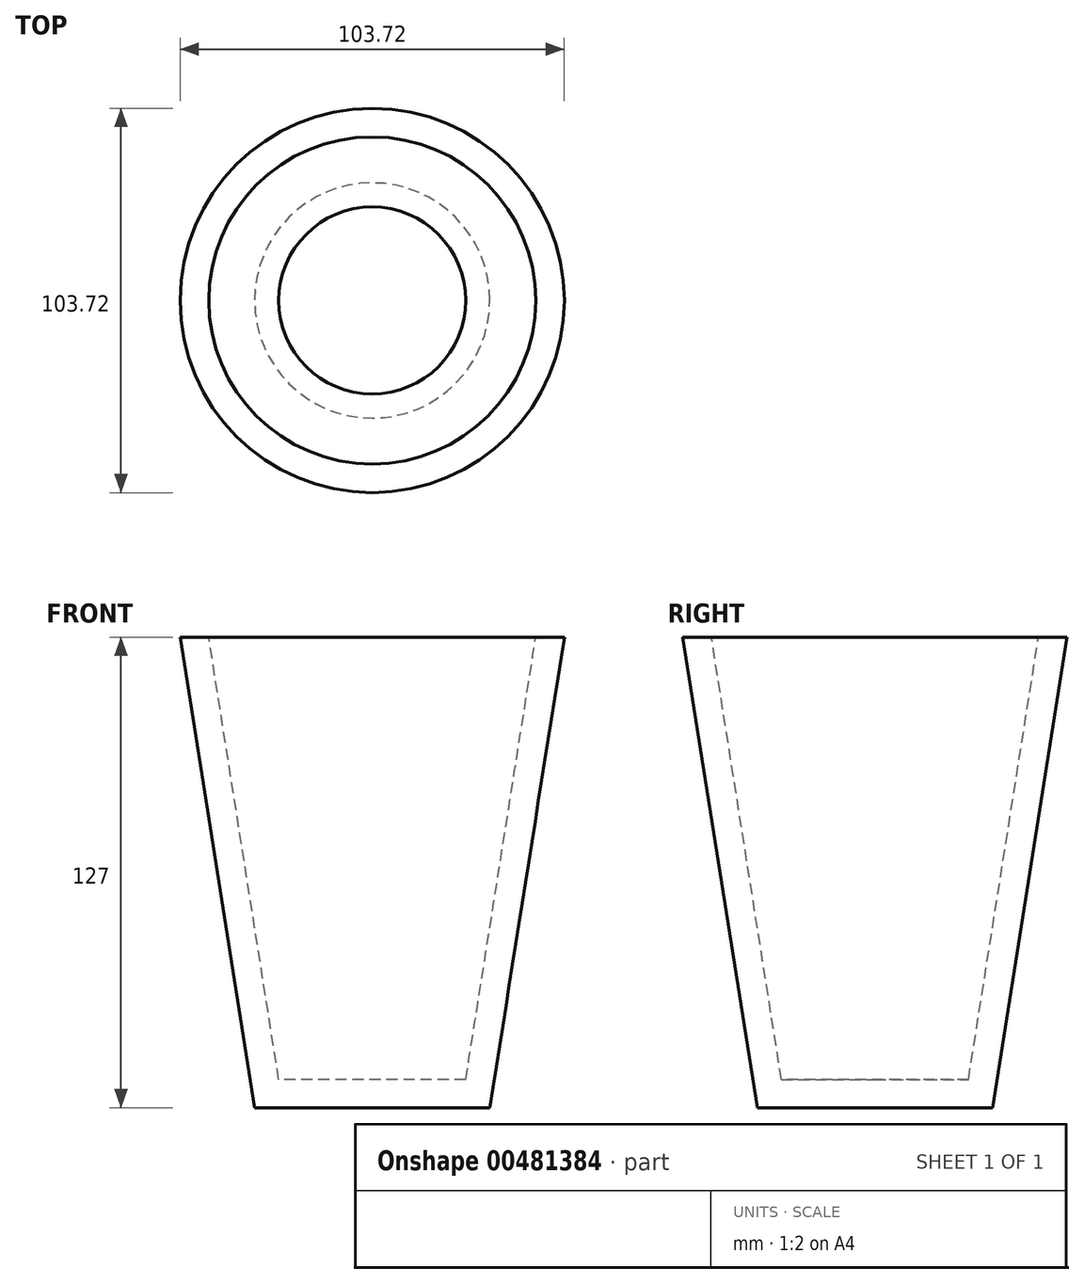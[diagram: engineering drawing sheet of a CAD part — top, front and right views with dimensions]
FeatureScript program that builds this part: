
annotation { "Feature Type Name" : "Feature", "Feature Type Description" : "" }
export const myFeature = defineFeature(function(context is Context, id is Id, definition is map)
    precondition{}
    {
        {
            var Q0;
            Q0=qCreatedBy(makeId("Top.planeOp"),FACE);
            var sketch = newSketch(context, id + "F0", { "sketchPlane" : qUnion([Q0])});
            skCircle(sketch, "E0", {"center": v(0, 0) * mm, "radius": 31.75 * mm});
            skSolve(sketch);
        }
        {
            var Q0;
            Q0 = qSketchRegion(id + "F0", true);
            extrude(context, id + "F1", {"entities" : qUnion([Q0]), "depth" : 127 * mm, "hasDraft" : true, "draftAngle" : 9 * degree});
        }
        {
            var Q0;
            Q0=makeQuery(id+"F1.opExtrude","CAP_FACE",FACE,{"disambiguationData":[OSD([sQuery(id+"F0.wireOp",EDGE,"E0")])],"isStart":false});
            var Q1;
            Q1=makeQuery(id+"F1.opExtrude","SWEPT_BODY",BODY,{"disambiguationData":[OSD([sQuery(id+"F0.wireOp",EDGE,"E0")])]});
            shell(context, id + "F2", {"entities" : qUnion([Q0]), "parts" : qUnion([Q1]), "thickness" : 7.62 * mm});
        }
    });
